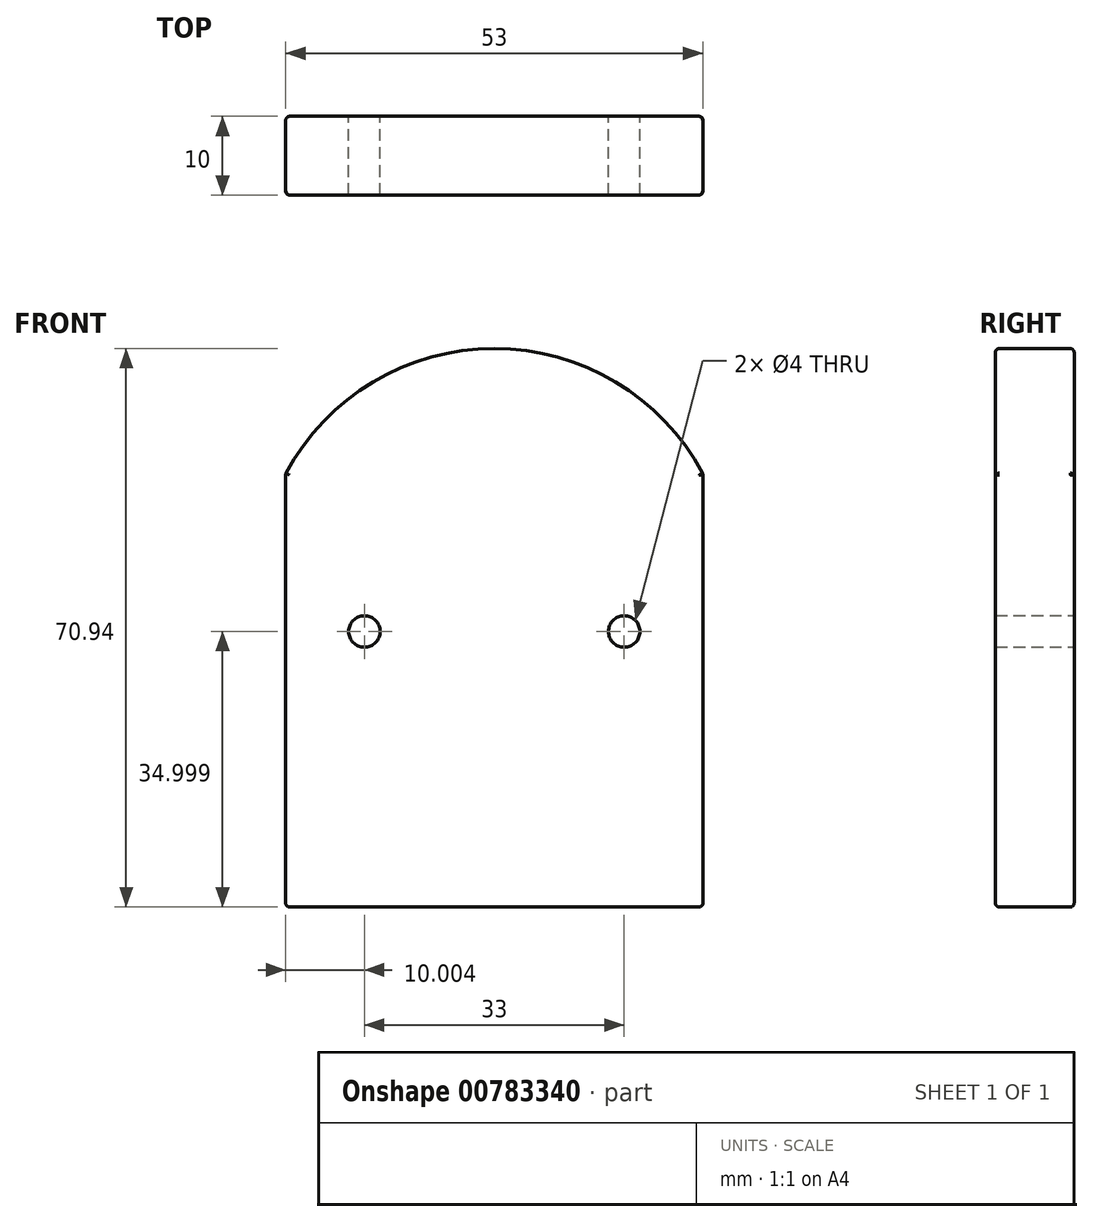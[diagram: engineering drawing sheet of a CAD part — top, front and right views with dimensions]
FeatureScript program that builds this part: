
annotation { "Feature Type Name" : "Feature", "Feature Type Description" : "" }
export const myFeature = defineFeature(function(context is Context, id is Id, definition is map)
    precondition{}
    {
        {
            var Q0;
            Q0=qCreatedBy(makeId("Front.planeOp"),FACE);
            var sketch = newSketch(context, id + "F0", { "sketchPlane" : qUnion([Q0])});
            skLineSegment(sketch, "E0", {"start": v(-53.36, 55.1) * mm, "end": v(-53.36, 0.1) * mm});
            skLineSegment(sketch, "E1", {"start": v(-0.36, 55.1) * mm, "end": v(-0.36, 0.1) * mm});
            skLineSegment(sketch, "E2", {"start": v(-0.36, 0.1) * mm, "end": v(-53.36, 0.1) * mm});
            skArc(sketch, "E3", {"start": v(-0.36, 55.1) * mm, "mid": v(-26.86, 71.04) * mm, "end": v(-53.36, 55.1) * mm});
            skSolve(sketch);
        }
        {
            var Q0;
            Q0=makeQuery(id+"F0.imprint","IMPRINT",FACE,{"disambiguationData":[TD([[makeQuery(id+"F0.imprint","IMPRINT",EDGE,{"derivedFrom":sQuery(id+"F0.wireOp",EDGE,"E0")}),1.0]])]});
            extrude(context, id + "F1", {"entities" : qUnion([Q0]), "depth" : 10 * mm, "offsetDistance" : 25 * mm});
        }
        {
            var Q0;
            Q0=qCreatedBy(makeId("Front.planeOp"),FACE);
            var sketch = newSketch(context, id + "F2", { "sketchPlane" : qUnion([Q0])});
            skCircle(sketch, "E4", {"center": v(-43.36, 35.1) * mm, "radius": 2 * mm});
            skCircle(sketch, "E5", {"center": v(-10.36, 35.1) * mm, "radius": 2 * mm});
            skSolve(sketch);
        }
        {
            var Q0;
            Q0 = qSketchRegion(id + "F2", true);
            extrude(context, id + "F3", {"entities" : qUnion([Q0]), "operationType" : NewBodyOperationType.REMOVE, "endBound" : BoundingType.THROUGH_ALL, "depth" : 25 * mm, "offsetDistance" : 25 * mm});
        }
        {
            var Q0;
            Q0=makeQuery(id+"F1.opExtrude","CAP_EDGE",EDGE,{"disambiguationData":[OSD([sQuery(id+"F0.wireOp",EDGE,"E3")])],"isStart":false});
            var Q1;
            Q1=makeQuery(id+"F1.opExtrude","CAP_EDGE",EDGE,{"disambiguationData":[OSD([sQuery(id+"F0.wireOp",EDGE,"E1")])],"isStart":false});
            var Q2;
            Q2=makeQuery(id+"F1.opExtrude","CAP_EDGE",EDGE,{"disambiguationData":[OSD([sQuery(id+"F0.wireOp",EDGE,"E0")])],"isStart":false});
            var Q3;
            Q3=makeQuery(id+"F1.opExtrude","CAP_EDGE",EDGE,{"disambiguationData":[OSD([sQuery(id+"F0.wireOp",EDGE,"E2")])],"isStart":false});
            fillet(context, id + "F4", {"entities" : qUnion([Q0, Q1, Q2, Q3]), "tangentPropagation" : true, "radius" : 0.5 * mm, "defaultsChanged" : true, "vertexSettings" : [], "allowEdgeOverflow" : false});
        }
        {
            var Q0;
            Q0=makeQuery(id+"F1.opExtrude","SWEPT_EDGE",EDGE,{"disambiguationData":[OSD([sQuery(id+"F0.wireOp",EDGE,"E1"),sQuery(id+"F0.wireOp",EDGE,"E3")])]});
            fillet(context, id + "F5", {"entities" : qUnion([Q0]), "tangentPropagation" : true, "crossSection" : FilletCrossSection.CURVATURE, "radius" : 0.5 * mm, "magnitude" : 0.5, "defaultsChanged" : false, "vertexSettings" : []});
        }
        {
            var Q0;
            Q0=makeQuery(id+"F1.opExtrude","SWEPT_EDGE",EDGE,{"disambiguationData":[OSD([sQuery(id+"F0.wireOp",EDGE,"E1"),sQuery(id+"F0.wireOp",EDGE,"E2")])]});
            var Q1;
            Q1=makeQuery(id+"F1.opExtrude","SWEPT_EDGE",EDGE,{"disambiguationData":[OSD([sQuery(id+"F0.wireOp",EDGE,"E0"),sQuery(id+"F0.wireOp",EDGE,"E2")])]});
            fillet(context, id + "F6", {"entities" : qUnion([Q0, Q1]), "tangentPropagation" : true, "radius" : 0.5 * mm, "defaultsChanged" : false, "vertexSettings" : [], "allowEdgeOverflow" : false});
        }
        {
            var Q0;
            Q0=makeQuery(id+"F1.opExtrude","CAP_EDGE",EDGE,{"disambiguationData":[OSD([sQuery(id+"F0.wireOp",EDGE,"E2")])],"isStart":true});
            var Q1;
            Q1=makeQuery(id+"F1.opExtrude","SWEPT_EDGE",EDGE,{"disambiguationData":[OSD([sQuery(id+"F0.wireOp",EDGE,"E0"),sQuery(id+"F0.wireOp",EDGE,"E3")])]});
            fillet(context, id + "F7", {"entities" : qUnion([Q0, Q1]), "tangentPropagation" : true, "radius" : 0.5 * mm, "defaultsChanged" : false, "vertexSettings" : [], "allowEdgeOverflow" : false});
        }
    });
